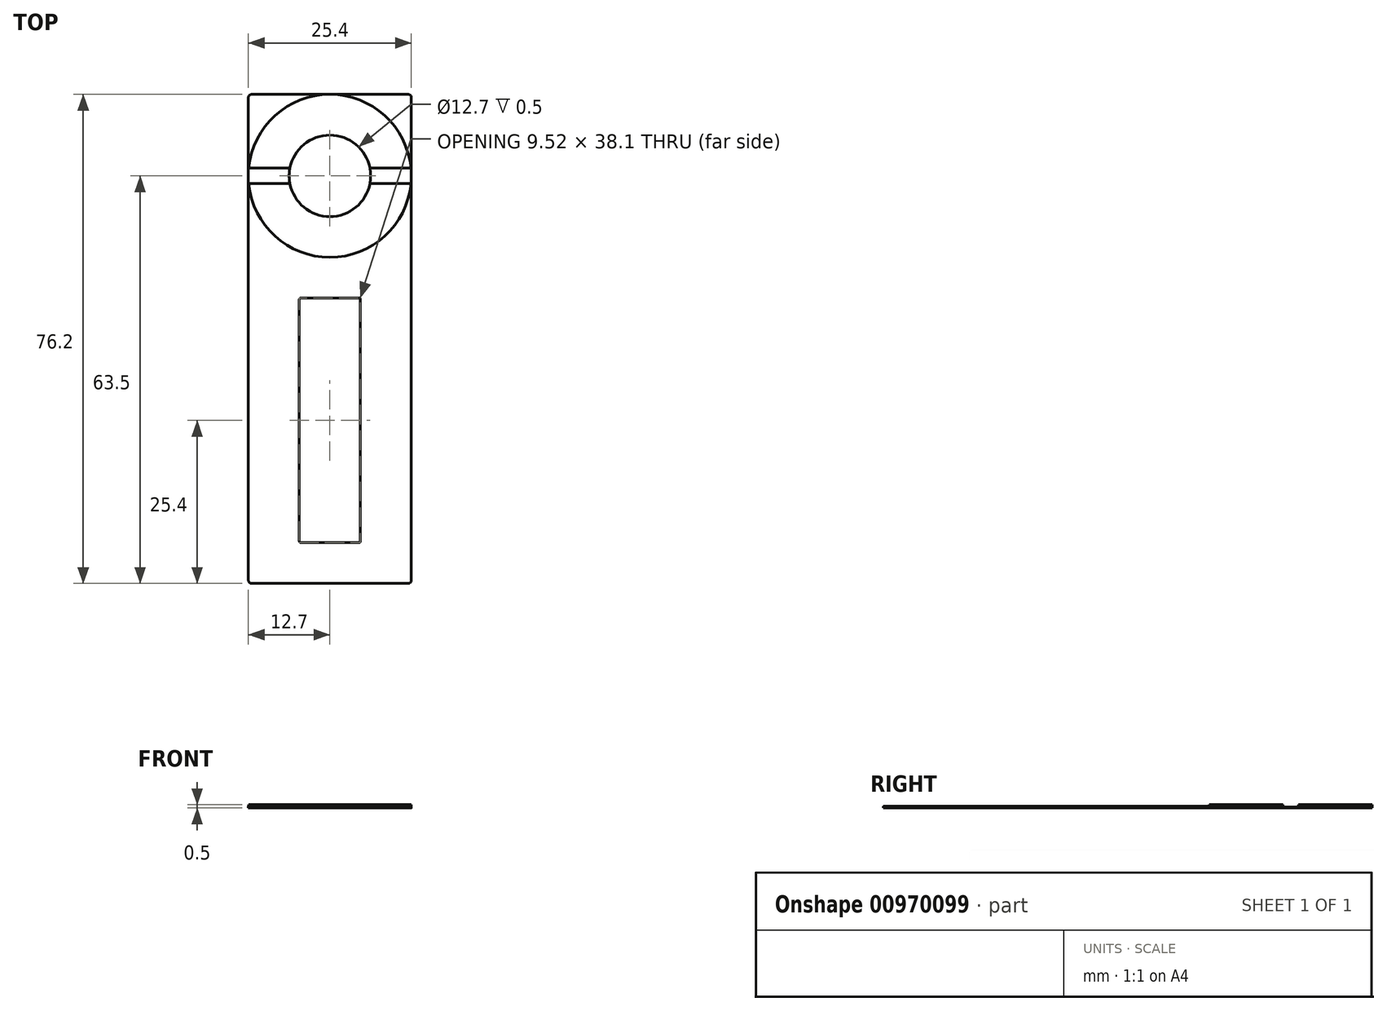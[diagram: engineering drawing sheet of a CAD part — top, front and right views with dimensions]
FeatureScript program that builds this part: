
annotation { "Feature Type Name" : "Feature", "Feature Type Description" : "" }
export const myFeature = defineFeature(function(context is Context, id is Id, definition is map)
    precondition{}
    {
        {
            assignVariable(context, id + "F0", {"name" : "Thickness", "anyValue" : .25});
        }
        {
            assignVariable(context, id + "F1", {"name" : "GrooveDepth", "anyValue" : 3 / 8});
        }
        {
            assignVariable(context, id + "F2", {"name" : "ExteriorFillet", "anyValue" : .5});
        }
        {
            assignVariable(context, id + "F3", {"name" : "SlotFillet", "anyValue" : 0.2});
        }
        {
            var Q0;
            Q0=qCreatedBy(makeId("Top.planeOp"),FACE);
            var sketch = newSketch(context, id + "F4", { "sketchPlane" : qUnion([Q0])});
            skLineSegment(sketch, "E0.bottom", {"start": v(0, 0) * mm, "end": v(25.4, 0) * mm});
            skLineSegment(sketch, "E0.top", {"start": v(0, 76.2) * mm, "end": v(25.4, 76.2) * mm});
            skLineSegment(sketch, "E0.left", {"start": v(0, 0) * mm, "end": v(0, 76.2) * mm});
            skLineSegment(sketch, "E0.right", {"start": v(25.4, 0) * mm, "end": v(25.4, 76.2) * mm});
            skSolve(sketch);
        }
        {
            var Q0;
            Q0 = qSketchRegion(id + "F4", true);
            extrude(context, id + "F5", {"entities" : qUnion([Q0]), "depth" : (getVariable(context, 'Thickness')) * mm, "offsetDistance" : 25.4 * mm});
        }
        {
            var Q0;
            Q0=makeQuery(id+"F5.opExtrude","CAP_FACE",FACE,{"disambiguationData":[OSD([sQuery(id+"F4.wireOp",EDGE,"E0.bottom"),sQuery(id+"F4.wireOp",EDGE,"E0.top"),sQuery(id+"F4.wireOp",EDGE,"E0.left"),sQuery(id+"F4.wireOp",EDGE,"E0.right")])],"isStart":false});
            var sketch = newSketch(context, id + "F6", { "sketchPlane" : qUnion([Q0])});
            skCircle(sketch, "E1", {"center": v(12.7, 63.5) * mm, "radius": 12.7 * mm});
            skSolve(sketch);
        }
        {
            var Q0;
            Q0 = qSketchRegion(id + "F6", true);
            extrude(context, id + "F7", {"entities" : qUnion([Q0]), "operationType" : NewBodyOperationType.ADD, "depth" : (getVariable(context, 'Thickness')) * mm, "offsetDistance" : 25.4 * mm});
        }
        {
            var Q0;
            Q0=makeQuery(id+"F7.opExtrude","CAP_FACE",FACE,{"disambiguationData":[OSD([sQuery(id+"F6.wireOp",EDGE,"E1")])],"isStart":false});
            var sketch = newSketch(context, id + "F8", { "sketchPlane" : qUnion([Q0])});
            skCircle(sketch, "E2", {"center": v(12.7, 63.5) * mm, "radius": 6.35 * mm});
            skSolve(sketch);
        }
        {
            var Q0;
            Q0 = qSketchRegion(id + "F8", true);
            extrude(context, id + "F9", {"entities" : qUnion([Q0]), "operationType" : NewBodyOperationType.REMOVE, "endBound" : BoundingType.THROUGH_ALL, "oppositeDirection" : true, "depth" : 25.4 * mm, "offsetDistance" : 25.4 * mm});
        }
        {
            var Q0;
            Q0=makeQuery(id+"F7.opExtrude","CAP_FACE",FACE,{"disambiguationData":[OSD([sQuery(id+"F6.wireOp",EDGE,"E1")])],"isStart":false});
            var sketch = newSketch(context, id + "F10", { "sketchPlane" : qUnion([Q0])});
            skLineSegment(sketch, "E3.bottom", {"start": v(0, 64.7) * mm, "end": v(25.4, 64.7) * mm});
            skLineSegment(sketch, "E3.top", {"start": v(0, 62.3) * mm, "end": v(25.4, 62.3) * mm});
            skLineSegment(sketch, "E3.left", {"start": v(0, 64.7) * mm, "end": v(0, 62.3) * mm});
            skLineSegment(sketch, "E3.right", {"start": v(25.4, 64.7) * mm, "end": v(25.4, 62.3) * mm});
            skPoint(sketch, "E4", {"position": v(0, 63.5) * mm});
            skPoint(sketch, "E5", {"position": v(25.4, 63.5) * mm});
            skSolve(sketch);
        }
        {
            var Q0;
            Q0 = qSketchRegion(id + "F10", true);
            extrude(context, id + "F11", {"entities" : qUnion([Q0]), "operationType" : NewBodyOperationType.REMOVE, "oppositeDirection" : true, "depth" : (getVariable(context, 'GrooveDepth')) * mm, "offsetDistance" : 25.4 * mm});
        }
        {
            var Q0;
            {var subQ0=sQuery(id+"F4.wireOp",EDGE,"E0.left");var subQ1=sQuery(id+"F4.wireOp",EDGE,"E0.right");var subQ2=sQuery(id+"F4.wireOp",EDGE,"E0.bottom");var subQ3=makeQuery(id+"F5.opExtrude","CAP_FACE",FACE,{"disambiguationData":[OSD([subQ2,sQuery(id+"F4.wireOp",EDGE,"E0.top"),subQ0,subQ1])],"isStart":false});Q0=makeQuery(id+"F7.boolean.opBoolean","SPLIT",FACE,{"disambiguationData":[TD([makeQuery(id+"F5.opExtrude","SWEPT_FACE",FACE,{"disambiguationData":[OSD([subQ2])]}),subQ3,makeQuery(id+"F5.opExtrude","SWEPT_FACE",FACE,{"disambiguationData":[OSD([subQ0])]}),makeQuery(id+"F5.opExtrude","SWEPT_FACE",FACE,{"disambiguationData":[OSD([subQ1])]}),makeQuery(id+"F7.opExtrude","SWEPT_FACE",FACE,{"disambiguationData":[OSD([sQuery(id+"F6.wireOp",EDGE,"E1")])]})])],"derivedFrom":subQ3});}
            var sketch = newSketch(context, id + "F12", { "sketchPlane" : qUnion([Q0])});
            skLineSegment(sketch, "E6.bottom", {"start": v(7.94, 44.45) * mm, "end": v(17.46, 44.45) * mm});
            skLineSegment(sketch, "E6.top", {"start": v(7.94, 6.35) * mm, "end": v(17.46, 6.35) * mm});
            skLineSegment(sketch, "E6.left", {"start": v(7.94, 44.45) * mm, "end": v(7.94, 6.35) * mm});
            skLineSegment(sketch, "E6.right", {"start": v(17.46, 44.45) * mm, "end": v(17.46, 6.35) * mm});
            skPoint(sketch, "E7", {"position": v(12.7, 6.35) * mm});
            skPoint(sketch, "E8", {"position": v(12.7, 0) * mm});
            skSolve(sketch);
        }
        {
            var Q0;
            Q0 = qSketchRegion(id + "F12", true);
            extrude(context, id + "F13", {"entities" : qUnion([Q0]), "operationType" : NewBodyOperationType.REMOVE, "endBound" : BoundingType.THROUGH_ALL, "oppositeDirection" : true, "depth" : 25.4 * mm, "offsetDistance" : 25.4 * mm});
        }
        {
            var Q0;
            Q0=makeQuery(id+"F5.opExtrude","SWEPT_EDGE",EDGE,{"disambiguationData":[OSD([sQuery(id+"F4.wireOp",EDGE,"E0.bottom"),sQuery(id+"F4.wireOp",EDGE,"E0.right")])]});
            var Q1;
            Q1=makeQuery(id+"F5.opExtrude","SWEPT_EDGE",EDGE,{"disambiguationData":[OSD([sQuery(id+"F4.wireOp",EDGE,"E0.bottom"),sQuery(id+"F4.wireOp",EDGE,"E0.left")])]});
            var Q2;
            Q2=makeQuery(id+"F5.opExtrude","SWEPT_EDGE",EDGE,{"disambiguationData":[OSD([sQuery(id+"F4.wireOp",EDGE,"E0.top"),sQuery(id+"F4.wireOp",EDGE,"E0.right")])]});
            var Q3;
            Q3=makeQuery(id+"F5.opExtrude","SWEPT_EDGE",EDGE,{"disambiguationData":[OSD([sQuery(id+"F4.wireOp",EDGE,"E0.top"),sQuery(id+"F4.wireOp",EDGE,"E0.left")])]});
            fillet(context, id + "F14", {"entities" : qUnion([Q0, Q1, Q2, Q3]), "radius" : (getVariable(context, 'ExteriorFillet')) * mm, "tangentPropagation" : true, "allowEdgeOverflow" : false});
        }
        {
            var Q0;
            Q0=makeQuery(id+"F13.boolean.opBoolean","COPY",EDGE,{"derivedFrom":makeQuery(id+"F13.opExtrude","SWEPT_EDGE",EDGE,{"disambiguationData":[OSD([sQuery(id+"F12.wireOp",EDGE,"E6.top"),sQuery(id+"F12.wireOp",EDGE,"E6.right")])]})});
            var Q1;
            Q1=makeQuery(id+"F13.boolean.opBoolean","COPY",EDGE,{"derivedFrom":makeQuery(id+"F13.opExtrude","SWEPT_EDGE",EDGE,{"disambiguationData":[OSD([sQuery(id+"F12.wireOp",EDGE,"E6.top"),sQuery(id+"F12.wireOp",EDGE,"E6.left")])]})});
            var Q2;
            Q2=makeQuery(id+"F13.boolean.opBoolean","COPY",EDGE,{"derivedFrom":makeQuery(id+"F13.opExtrude","SWEPT_EDGE",EDGE,{"disambiguationData":[OSD([sQuery(id+"F12.wireOp",EDGE,"E6.bottom"),sQuery(id+"F12.wireOp",EDGE,"E6.left")])]})});
            var Q3;
            Q3=makeQuery(id+"F13.boolean.opBoolean","COPY",EDGE,{"derivedFrom":makeQuery(id+"F13.opExtrude","SWEPT_EDGE",EDGE,{"disambiguationData":[OSD([sQuery(id+"F12.wireOp",EDGE,"E6.bottom"),sQuery(id+"F12.wireOp",EDGE,"E6.right")])]})});
            fillet(context, id + "F15", {"entities" : qUnion([Q0, Q1, Q2, Q3]), "radius" : (getVariable(context, 'SlotFillet')) * mm, "tangentPropagation" : true, "allowEdgeOverflow" : false});
        }
    });
